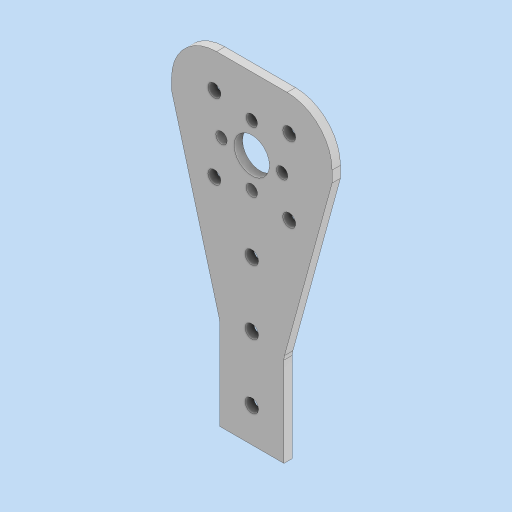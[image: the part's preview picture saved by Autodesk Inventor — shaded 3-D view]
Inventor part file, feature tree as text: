
AUTODESK INVENTOR PART (.ipt)
format: ipt  version: 2024 (Build 280153000, 153)  size: 259,584 bytes
history: native  units: in
note: dims shown in document units (in); Inventor stores cm internally (conversion verified against a paired STEP export)
features: sketch x4, fillet x3, extrude x2, hole x2, pattern_circular x2
ambient origin geometry x8: Origin, YZ Plane, XZ Plane, XY Plane, X Axis, Y Axis, Z Axis, Center Point
bodies: Solid1 (feature_tree)
feature tree (13):
  extrude  "Extrusion1"  Depth=2.5in
  fillet  "Fillet11"  Radius=0.209in
  fillet  "Fillet12"  Radius=1.125in
  hole  "Hole1"  [1 undecoded]
  pattern_circular  "Circular Pattern1"  [2 undecoded]
  hole  "Hole2"  [1 undecoded]
  pattern_circular  "Circular Pattern2"  Angle=90.0deg  [1 undecoded]
  fillet  "Fillet16"  Radius=1.5748in
  extrude  "Extrusion2"  Depth=1.0in
  sketch  "Sketch1"  dims[d0=2.5in d2=0.3189in d3=0.209in d5=1.125in]
  sketch  "Sketch3"  dims[d10=0.13in d11=0.0in d22=0.7in]
  sketch  "Sketch4"  dims[d23=0.7in]
  sketch  "Sketch5"  dims[d26=1.2598in d27=0.6299in d28=0.9449in d29=0.177in d30=0.75in d31=0.37in d32=0.25in d33=90.0deg d34=0.559in d35=0.8108in d36=90.0deg d37=1.5748in d38=360.0deg d40=0.9449in d41=1.2598in d42=1.65in d43=0.201in d44=0.432in d45=0.385in d46=0.25in d47=0.5635in d48=0.64in d49=0.8108in d50=3.25in d51=1.5748in d52=360.0deg d54=0.209in d55=2.5in d58=45.0deg d59=1.0in d60=1.0in d61=1.0in d63=0.25in d64=0.5512in d65=1.0in d66=0.0in d16=0.0in d17=0.0in d18=0.0in d19=0.0in d20=0.0in d21=0.0in]
note: 5 required parameter values undecoded (feature->parameter linkage not recoverable at this tier; creation-order binding heuristic only, values carry confidence <= 0.55)
